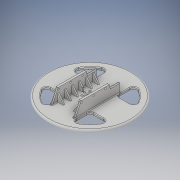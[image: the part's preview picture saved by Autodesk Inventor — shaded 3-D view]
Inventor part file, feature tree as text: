
AUTODESK INVENTOR PART (.ipt)
format: ipt  version: 2018 (Build 220112000, 112)  size: 1,280,512 bytes
history: native  units: in
note: dims shown in document units (in); Inventor stores cm internally (conversion verified against a paired STEP export)
features: extrude x8, sketch x7, fillet x5, projected_geometry x4, pattern_linear x2, rib x1, mirror x1, hole x1
ambient origin geometry x8: Origin, YZ Plane, XZ Plane, XY Plane, X Axis, Y Axis, Z Axis, Center Point
bodies: Solid1 (feature_tree)
feature tree (29):
  sketch  "Sketch1"  dims[d1=1.1811in d2=1.9921in]
  extrude  "Extrusion1"  Depth=1.9921in
  extrude  "Extrusion2"  Depth=0.1575in TaperAngle=0.0deg
  sketch  "Sketch2"  dims[d3=0.1083in d4=0.1575in d5=0.0in]
  extrude  "Extrusion3"  Depth=1.1811in
  extrude  "Extrusion4"  Depth=1.5748in TaperAngle=0.0deg
  extrude  "Extrusion5"  Depth=1.5748in TaperAngle=0.0deg
  rib  "Rib1"
  pattern_linear  "Rectangular Pattern1"  Count1=4 Spacing1=0.0in
  pattern_linear  "Rectangular Pattern2"  Spacing1=0.0394in  [1 undecoded]
  mirror  "Mirror1"
  fillet  "Fillet1"  Radius=0.3937in
  fillet  "Fillet2"  Radius=0.3937in
  sketch  "Sketch8"  dims[d12=0.1718in d13=1.5748in d14=0.0in d15=1.5748in d16=0.0in]
  extrude  "Extrusion9"  Depth=0.0394in
  hole  "Hole1"  [1 undecoded]
  extrude  "Extrusion10"  Depth=0.0394in
  fillet  "Fillet5"  Radius=0.6299in
  extrude  "Extrusion11"  Depth=0.0394in TaperAngle=360.0deg
  fillet  "Fillet6"  Radius=0.3937in
  fillet  "Fillet7"  Radius=0.1969in
  projected_geometry  "Projected Loop1"
  sketch  "Sketch3"  dims[d6=1.5748in d7=0.0in d8=1.1811in]
  projected_geometry  "Projected Loop2"
  sketch  "Sketch4"  dims[d9=180.0deg d10=1.5748in d11=0.0in]
  projected_geometry  "Projected Loop3"
  projected_geometry  "Projected Loop4"
  sketch  "Sketch9"  dims[d17=0.4331in]
  sketch  "Sketch10"  dims[d18=0.315in d19=0.0394in d20=0.0787in d21=0.0in d22=0.0in d23=0.0394in d24=0.0394in d25=1.5748in d27=0.3937in d28=1.1811in d30=0.3937in d50=0.0787in d51=0.0394in d63=0.3543in d64=0.6299in d65=3.1496in d67=360.0deg d69=0.3937in d70=0.0in d71=0.1142in d72=0.2362in d73=0.1575in d74=0.0787in d75=90.0deg d76=0.315in d77=0.8108in d78=0.1969in d79=0.1969in d80=0.0in d81=0.0in d82=0.0394in d83=0.0118in d84=0.315in d85=1.4764in d86=0.7382in d87=0.3937in d88=0.0in d89=0.1969in d90=0.0394in]
note: 2 required parameter values undecoded (feature->parameter linkage not recoverable at this tier; creation-order binding heuristic only, values carry confidence <= 0.55)
